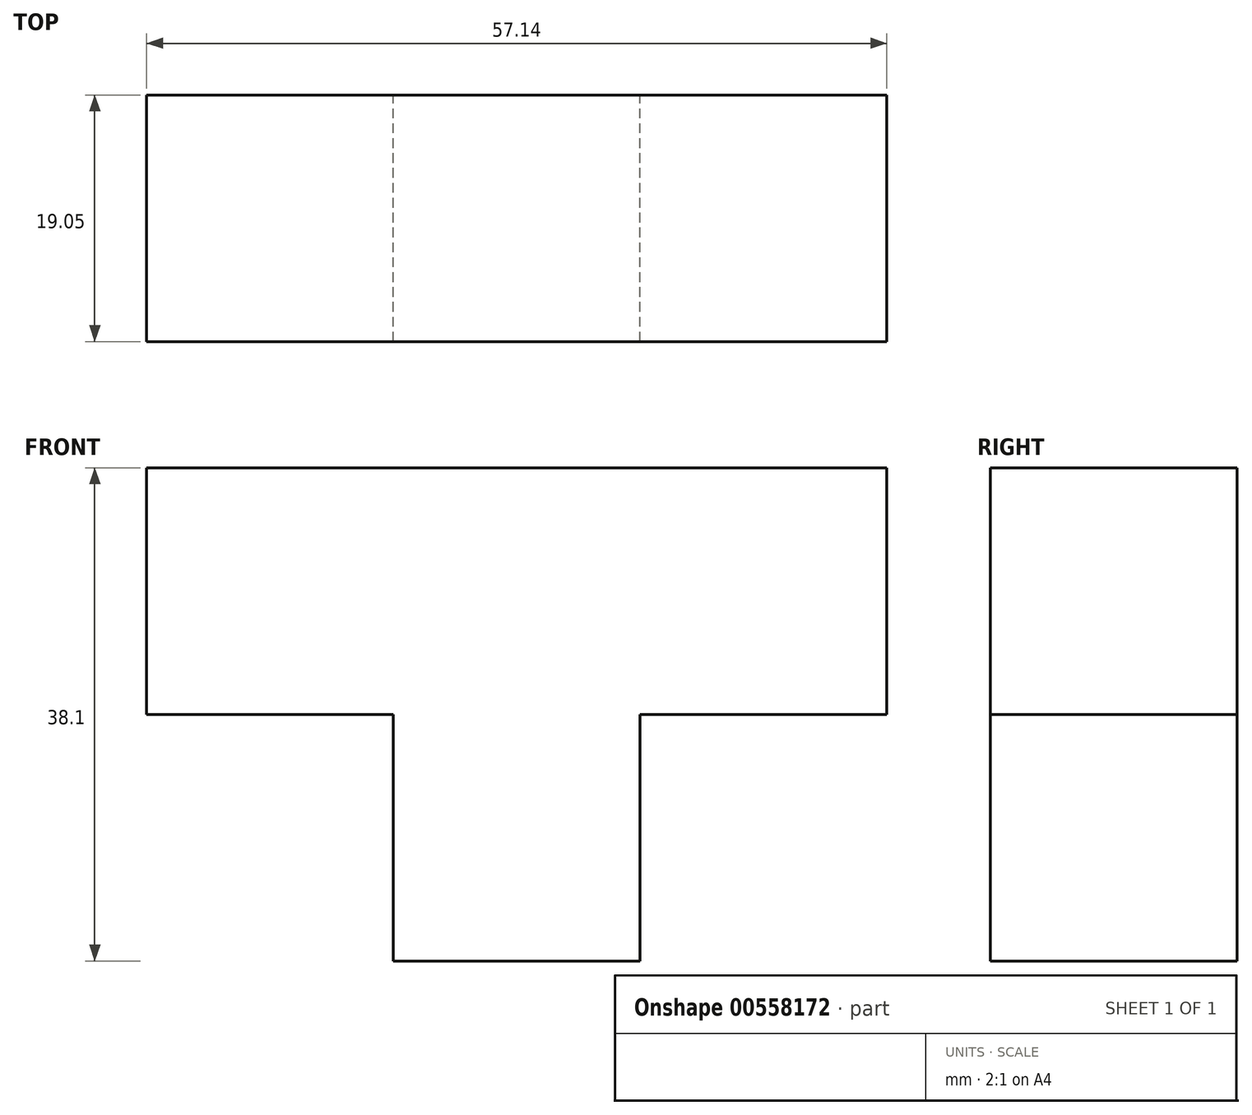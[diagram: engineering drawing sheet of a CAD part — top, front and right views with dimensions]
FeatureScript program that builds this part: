
annotation { "Feature Type Name" : "Feature", "Feature Type Description" : "" }
export const myFeature = defineFeature(function(context is Context, id is Id, definition is map)
    precondition{}
    {
        {
            var Q0;
            Q0=qCreatedBy(makeId("Front.planeOp"),FACE);
            var sketch = newSketch(context, id + "F0", { "sketchPlane" : qUnion([Q0])});
            skLineSegment(sketch, "E0", {"start": v(0, 0) * mm, "end": v(-28.58, 0) * mm});
            skLineSegment(sketch, "E1", {"start": v(0, 0) * mm, "end": v(28.58, 0) * mm});
            skLineSegment(sketch, "E2", {"start": v(28.58, 0) * mm, "end": v(28.58, -19.05) * mm});
            skLineSegment(sketch, "E3", {"start": v(28.58, -19.05) * mm, "end": v(9.53, -19.05) * mm});
            skLineSegment(sketch, "E4", {"start": v(9.53, -19.05) * mm, "end": v(9.53, -38.1) * mm});
            skLineSegment(sketch, "E5", {"start": v(9.53, -38.1) * mm, "end": v(-9.52, -38.1) * mm});
            skLineSegment(sketch, "E6", {"start": v(-9.52, -38.1) * mm, "end": v(-9.52, -19.05) * mm});
            skLineSegment(sketch, "E7", {"start": v(-9.52, -19.05) * mm, "end": v(-28.58, -19.05) * mm});
            skLineSegment(sketch, "E8", {"start": v(-28.58, -19.05) * mm, "end": v(-28.58, 0) * mm});
            skSolve(sketch);
        }
        {
            var Q0;
            Q0 = qSketchRegion(id + "F0", true);
            extrude(context, id + "F1", {"entities" : qUnion([Q0]), "depth" : 19.05 * mm, "offsetDistance" : 25.4 * mm});
        }
    });
